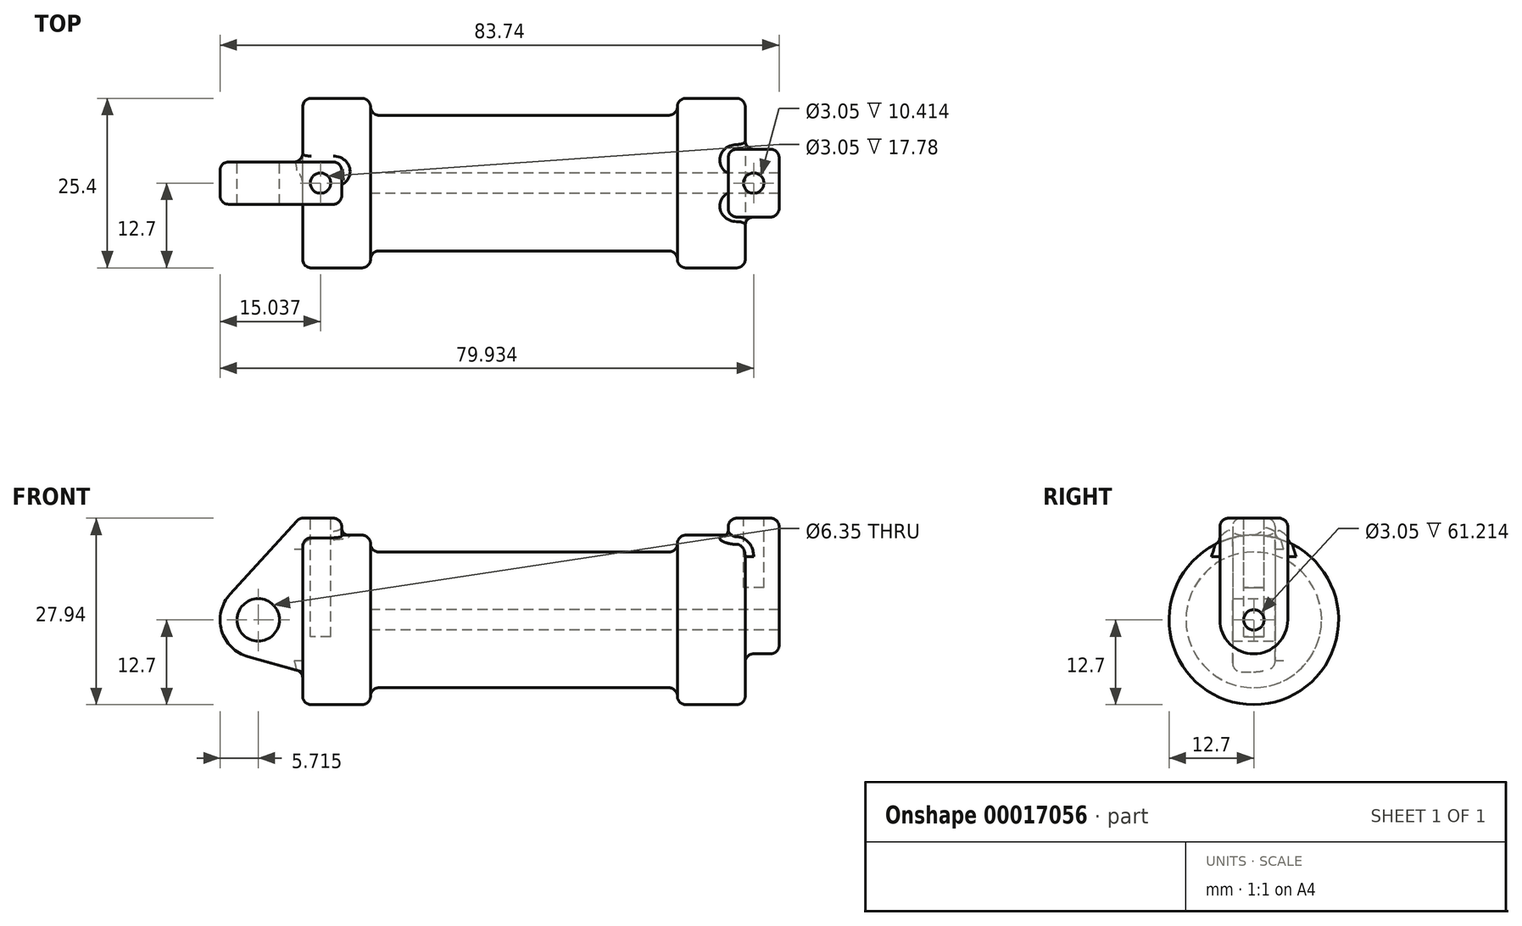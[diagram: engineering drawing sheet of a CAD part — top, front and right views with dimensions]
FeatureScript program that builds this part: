
annotation { "Feature Type Name" : "Feature", "Feature Type Description" : "" }
export const myFeature = defineFeature(function(context is Context, id is Id, definition is map)
    precondition{}
    {
        {
            var Q0;
            Q0=qCreatedBy(makeId("Front.planeOp"),FACE);
            var sketch = newSketch(context, id + "F0", { "sketchPlane" : qUnion([Q0])});
            skLineSegment(sketch, "E0", {"start": v(0, 0) * mm, "end": v(0, 12.7) * mm});
            skLineSegment(sketch, "E1", {"start": v(0, 12.7) * mm, "end": v(10.16, 12.7) * mm});
            skLineSegment(sketch, "E2", {"start": v(10.16, 12.7) * mm, "end": v(10.16, 10.16) * mm});
            skLineSegment(sketch, "E3", {"start": v(10.16, 10.16) * mm, "end": v(56.13, 10.16) * mm});
            skLineSegment(sketch, "E4", {"start": v(56.13, 10.16) * mm, "end": v(56.13, 12.7) * mm});
            skLineSegment(sketch, "E5", {"start": v(56.13, 12.7) * mm, "end": v(66.3, 12.7) * mm});
            skLineSegment(sketch, "E6", {"start": v(66.3, 12.7) * mm, "end": v(66.3, 0) * mm});
            skLineSegment(sketch, "E7", {"start": v(66.3, 0) * mm, "end": v(0, 0) * mm});
            skLineSegment(sketch, "E8", {"start": v(5.84, 15.24) * mm, "end": v(-0.5, 15.24) * mm});
            skLineSegment(sketch, "E9", {"start": v(-0.5, 15.24) * mm, "end": v(-10.88, 3.85) * mm});
            skLineSegment(sketch, "E10", {"start": v(0, 0) * mm, "end": v(-6.65, 0) * mm});
            skCircle(sketch, "E11", {"center": v(-6.65, 0) * mm, "radius": 5.72 * mm});
            skCircle(sketch, "E12", {"center": v(-6.65, 0) * mm, "radius": 3.18 * mm});
            skLineSegment(sketch, "E13", {"start": v(5.84, 15.24) * mm, "end": v(5.84, -9.4) * mm});
            skLineSegment(sketch, "E14", {"start": v(5.84, -9.4) * mm, "end": v(-8.18, -5.5) * mm});
            skSolve(sketch);
        }
        {
            var Q0;
            {var subQ6=sQuery(id+"F0.wireOp",EDGE,"E2");Q0=makeQuery(id+"F0.imprint","IMPRINT",FACE,{"disambiguationData":[TD([[makeQuery(id+"F0.imprint","IMPRINT",EDGE,{"derivedFrom":subQ6}),-1.0]])]});}
            var Q1;
            {var subQ5=sQuery(id+"F0.wireOp",EDGE,"E0");Q1=makeQuery(id+"F0.imprint","IMPRINT",FACE,{"disambiguationData":[TD([[makeQuery(id+"F0.imprint","IMPRINT",EDGE,{"derivedFrom":subQ5}),-1.0]])]});}
            var Q2;
            Q2=sQuery(id+"F0.wireOp",EDGE,"E7");
            revolve(context, id + "F1", {"entities" : qUnion([Q0, Q1]), "axis" : qUnion([Q2]), "revolveType" : RevolveType.FULL});
        }
        {
            var Q0;
            {var subQ8=sQuery(id+"F0.wireOp",EDGE,"E0");Q0=makeQuery(id+"F0.imprint","IMPRINT",FACE,{"disambiguationData":[TD([[makeQuery(id+"F0.imprint","IMPRINT",EDGE,{"derivedFrom":subQ8}),1.0]])]});}
            var Q1;
            {var subQ0=sQuery(id+"F0.wireOp",EDGE,"E12");Q1=makeQuery(id+"F0.imprint","IMPRINT",FACE,{"disambiguationData":[TD([[makeQuery(id+"F0.imprint","IMPRINT",EDGE,{"derivedFrom":subQ0}),-1.0]])]});}
            var Q2;
            {var subQ0=sQuery(id+"F0.wireOp",EDGE,"E14");Q2=makeQuery(id+"F0.imprint","IMPRINT",FACE,{"disambiguationData":[TD([[makeQuery(id+"F0.imprint","IMPRINT",EDGE,{"derivedFrom":subQ0}),-1.0]])]});}
            var Q3;
            {var subQ5=sQuery(id+"F0.wireOp",EDGE,"E0");Q3=makeQuery(id+"F0.imprint","IMPRINT",FACE,{"disambiguationData":[TD([[makeQuery(id+"F0.imprint","IMPRINT",EDGE,{"derivedFrom":subQ5}),-1.0]])]});}
            extrude(context, id + "F2", {"entities" : qUnion([Q0, Q1, Q2, Q3]), "operationType" : NewBodyOperationType.ADD, "endBound" : BoundingType.SYMMETRIC, "depth" : 6.35 * mm});
        }
        {
            var Q0;
            Q0=makeQuery(id+"F1.opRevolve","SWEPT_FACE",FACE,{"disambiguationData":[OSD([sQuery(id+"F0.wireOp",EDGE,"E6")])]});
            var sketch = newSketch(context, id + "F3", { "sketchPlane" : qUnion([Q0])});
            skCircle(sketch, "E15", {"center": v(0, 0) * mm, "radius": 5.08 * mm});
            skCircle(sketch, "E16", {"center": v(0, 0) * mm, "radius": 1.52 * mm});
            skLineSegment(sketch, "E17", {"start": v(-5.08, 0) * mm, "end": v(-5.08, 15.24) * mm});
            skLineSegment(sketch, "E18", {"start": v(-5.08, 15.24) * mm, "end": v(5.08, 15.24) * mm});
            skLineSegment(sketch, "E19", {"start": v(5.08, 15.24) * mm, "end": v(5.08, 0) * mm});
            skSolve(sketch);
        }
        {
            var Q0;
            Q0=makeQuery(id+"F3.imprint","IMPRINT",FACE,{"disambiguationData":[TD([[makeQuery(id+"F3.imprint","IMPRINT",EDGE,{"derivedFrom":sQuery(id+"F3.wireOp",EDGE,"E16")}),-1.0]])]});
            var Q1;
            {var subQ3=sQuery(id+"F3.wireOp",EDGE,"E17");var subQ5=sQuery(id+"F3.wireOp",EDGE,"E15");var subQ7=makeQuery(id+"F3.imprint","INTERSECT",VERTEX,{"derivedFrom":[subQ5,subQ3]});Q1=makeQuery(id+"F3.imprint","IMPRINT",FACE,{"disambiguationData":[TD([[makeQuery(id+"F3.imprint","IMPRINT",EDGE,{"disambiguationData":[TD([[subQ7,1.0]])],"derivedFrom":subQ5}),-1.0]])]});}
            var Q2;
            {var subQ5=sQuery(id+"F3.wireOp",EDGE,"E18");Q2=makeQuery(id+"F3.imprint","IMPRINT",FACE,{"disambiguationData":[TD([[makeQuery(id+"F3.imprint","IMPRINT",EDGE,{"derivedFrom":subQ5}),-1.0]])]});}
            extrude(context, id + "F4", {"entities" : qUnion([Q0, Q1, Q2]), "operationType" : NewBodyOperationType.ADD, "depth" : 5.08 * mm});
        }
        {
            var Q0;
            {var subQ0=sQuery(id+"F3.wireOp",EDGE,"E15");var subQ3=sQuery(id+"F3.wireOp",EDGE,"E17");var subQ4=makeQuery(id+"F3.imprint","INTERSECT",VERTEX,{"derivedFrom":[subQ0,subQ3]});var subQ5=makeQuery(id+"F3.imprint","IMPRINT",EDGE,{"disambiguationData":[TD([[subQ4,1.0]])],"derivedFrom":subQ0});var subQ10=sQuery(id+"F3.wireOp",EDGE,"E18");Q0=qUnion([makeQuery(id+"F3.imprint","IMPRINT",FACE,{"disambiguationData":[TD([[makeQuery(id+"F3.imprint","IMPRINT",EDGE,{"derivedFrom":sQuery(id+"F3.wireOp",EDGE,"E16")}),-1.0]])]}),makeQuery(id+"F3.imprint","IMPRINT",FACE,{"disambiguationData":[TD([[makeQuery(id+"F3.imprint","IMPRINT",EDGE,{"derivedFrom":subQ10}),-1.0]])]}),makeQuery(id+"F3.imprint","IMPRINT",FACE,{"disambiguationData":[TD([[subQ5,-1.0]])]})]);}
            extrude(context, id + "F5", {"entities" : qUnion([Q0]), "operationType" : NewBodyOperationType.ADD, "oppositeDirection" : true, "depth" : 2.54 * mm});
        }
        {
            var Q0;
            Q0=makeQuery(id+"F4.boolean.opBoolean","SPLIT",FACE,{"disambiguationData":[TD([makeQuery(id+"F4.opExtrude","SWEPT_FACE",FACE,{"disambiguationData":[OSD([sQuery(id+"F3.wireOp",EDGE,"E16")])]})])],"derivedFrom":makeQuery(id+"F1.opRevolve","SWEPT_FACE",FACE,{"disambiguationData":[OSD([sQuery(id+"F0.wireOp",EDGE,"E6")])]})});
            var Q1;
            Q1=makeQuery(id+"F1.opRevolve","SWEPT_FACE",FACE,{"disambiguationData":[OSD([sQuery(id+"F0.wireOp",EDGE,"E2")])]});
            extrude(context, id + "F6", {"entities" : qUnion([Q0]), "operationType" : NewBodyOperationType.REMOVE, "endBound" : BoundingType.UP_TO_SURFACE, "oppositeDirection" : true, "endBoundEntityFace" : qUnion([Q1]), "depth" : 25.4 * mm});
        }
        {
            var Q0;
            {var subQ0=sQuery(id+"F3.wireOp",EDGE,"E18");Q0=makeQuery(id+"F5.boolean.opBoolean","MERGE",FACE,{"derivedFrom":[makeQuery(id+"F4.opExtrude","SWEPT_FACE",FACE,{"disambiguationData":[OSD([subQ0])]}),makeQuery(id+"F5.opExtrude","SWEPT_FACE",FACE,{"disambiguationData":[OSD([subQ0])]})]});}
            var sketch = newSketch(context, id + "F7", { "sketchPlane" : qUnion([Q0])});
            skLineSegment(sketch, "E20", {"start": v(63.75, -5.08) * mm, "end": v(71.37, 5.08) * mm, "construction": true});
            skCircle(sketch, "E21", {"center": v(67.56, 0) * mm, "radius": 1.52 * mm});
            skSolve(sketch);
        }
        {
            var Q0;
            Q0=qSketchRegion(id+"F7",true);
            extrude(context, id + "F8", {"entities" : qUnion([Q0]), "operationType" : NewBodyOperationType.REMOVE, "oppositeDirection" : true, "depth" : 10.4 * mm});
        }
        {
            var Q0;
            Q0=makeQuery(id+"F2.opExtrude","SWEPT_FACE",FACE,{"disambiguationData":[OSD([sQuery(id+"F0.wireOp",EDGE,"E8")])]});
            var sketch = newSketch(context, id + "F9", { "sketchPlane" : qUnion([Q0])});
            skLineSegment(sketch, "E22", {"start": v(-0.5, -3.18) * mm, "end": v(5.84, 3.18) * mm, "construction": true});
            skCircle(sketch, "E23", {"center": v(2.67, 0) * mm, "radius": 1.52 * mm});
            skSolve(sketch);
        }
        {
            var Q0;
            Q0=makeQuery(id+"F9.imprint","IMPRINT",FACE,{"disambiguationData":[TD([[makeQuery(id+"F9.imprint","IMPRINT",EDGE,{"derivedFrom":sQuery(id+"F9.wireOp",EDGE,"E23")}),1.0]])]});
            extrude(context, id + "F10", {"entities" : qUnion([Q0]), "operationType" : NewBodyOperationType.REMOVE, "oppositeDirection" : true, "depth" : 17.78 * mm});
        }
        {
            var Q0;
            Q0=makeQuery(id+"F1.opRevolve","SWEPT_EDGE",EDGE,{"disambiguationData":[OSD([sQuery(id+"F0.wireOp",EDGE,"E2"),sQuery(id+"F0.wireOp",EDGE,"E3")])]});
            var Q1;
            Q1=makeQuery(id+"F1.opRevolve","SWEPT_EDGE",EDGE,{"disambiguationData":[OSD([sQuery(id+"F0.wireOp",EDGE,"E3"),sQuery(id+"F0.wireOp",EDGE,"E4")])]});
            fillet(context, id + "F11", {"entities" : qUnion([Q0, Q1]), "radius" : 1.27 * mm, "tangentPropagation" : true, "allowEdgeOverflow" : false});
        }
        {
            var Q0;
            Q0=makeQuery(id+"F2.opExtrude","SWEPT_EDGE",EDGE,{"disambiguationData":[OSD([sQuery(id+"F0.wireOp",EDGE,"E8"),sQuery(id+"F0.wireOp",EDGE,"E9")])]});
            var Q1;
            Q1=makeQuery(id+"F2.opExtrude","SWEPT_EDGE",EDGE,{"disambiguationData":[OSD([sQuery(id+"F0.wireOp",EDGE,"E8"),sQuery(id+"F0.wireOp",EDGE,"E13")])]});
            var Q2;
            Q2=makeQuery(id+"F2.opExtrude","CAP_EDGE",EDGE,{"disambiguationData":[OSD([sQuery(id+"F0.wireOp",EDGE,"E9")])],"isStart":false});
            var Q3;
            Q3=makeQuery(id+"F1.opRevolve","SWEPT_EDGE",EDGE,{"disambiguationData":[OSD([sQuery(id+"F0.wireOp",EDGE,"E0"),sQuery(id+"F0.wireOp",EDGE,"E1")])]});
            var Q4;
            Q4=makeQuery(id+"F1.opRevolve","SWEPT_EDGE",EDGE,{"disambiguationData":[OSD([sQuery(id+"F0.wireOp",EDGE,"E1"),sQuery(id+"F0.wireOp",EDGE,"E2")])]});
            var Q5;
            Q5=makeQuery(id+"F2.opExtrude","CAP_EDGE",EDGE,{"disambiguationData":[OSD([sQuery(id+"F0.wireOp",EDGE,"E13")])],"isStart":false});
            var Q6;
            Q6=makeQuery(id+"F2.opExtrude","CAP_EDGE",EDGE,{"disambiguationData":[OSD([sQuery(id+"F0.wireOp",EDGE,"E9")])],"isStart":true});
            var Q7;
            Q7=makeQuery(id+"F2.boolean.opBoolean","INTERSECT",EDGE,{"derivedFrom":[makeQuery(id+"F1.opRevolve","SWEPT_FACE",FACE,{"disambiguationData":[OSD([sQuery(id+"F0.wireOp",EDGE,"E1")])]}),makeQuery(id+"F2.opExtrude","CAP_FACE",FACE,{"disambiguationData":[OSD([sQuery(id+"F0.wireOp",EDGE,"E8"),sQuery(id+"F0.wireOp",EDGE,"E9"),sQuery(id+"F0.wireOp",EDGE,"E11"),sQuery(id+"F0.wireOp",EDGE,"E12"),sQuery(id+"F0.wireOp",EDGE,"E13"),sQuery(id+"F0.wireOp",EDGE,"E14")])],"isStart":true})]});
            var Q8;
            Q8=makeQuery(id+"F2.boolean.opBoolean","INTERSECT",EDGE,{"derivedFrom":[makeQuery(id+"F1.opRevolve","SWEPT_FACE",FACE,{"disambiguationData":[OSD([sQuery(id+"F0.wireOp",EDGE,"E0")])]}),makeQuery(id+"F2.opExtrude","CAP_FACE",FACE,{"disambiguationData":[OSD([sQuery(id+"F0.wireOp",EDGE,"E8"),sQuery(id+"F0.wireOp",EDGE,"E9"),sQuery(id+"F0.wireOp",EDGE,"E11"),sQuery(id+"F0.wireOp",EDGE,"E12"),sQuery(id+"F0.wireOp",EDGE,"E13"),sQuery(id+"F0.wireOp",EDGE,"E14")])],"isStart":true})]});
            var Q9;
            Q9=makeQuery(id+"F2.opExtrude","CAP_EDGE",EDGE,{"disambiguationData":[OSD([sQuery(id+"F0.wireOp",EDGE,"E8")])],"isStart":true});
            var Q10;
            Q10=makeQuery(id+"F2.opExtrude","CAP_EDGE",EDGE,{"disambiguationData":[OSD([sQuery(id+"F0.wireOp",EDGE,"E13")])],"isStart":true});
            var Q11;
            Q11=makeQuery(id+"F2.opExtrude","CAP_EDGE",EDGE,{"disambiguationData":[OSD([sQuery(id+"F0.wireOp",EDGE,"E8")])],"isStart":false});
            fillet(context, id + "F12", {"entities" : qUnion([Q0, Q1, Q2, Q3, Q4, Q5, Q6, Q7, Q8, Q9, Q10, Q11]), "radius" : 1.27 * mm, "tangentPropagation" : true, "allowEdgeOverflow" : false});
        }
        {
            var Q0;
            {var subQ0=sQuery(id+"F3.wireOp",EDGE,"E17");Q0=makeQuery(id+"F5.boolean.opBoolean","MERGE",FACE,{"derivedFrom":[makeQuery(id+"F4.opExtrude","SWEPT_FACE",FACE,{"disambiguationData":[OSD([subQ0])]}),makeQuery(id+"F5.opExtrude","SWEPT_FACE",FACE,{"disambiguationData":[OSD([subQ0])]})]});}
            var Q1;
            {var subQ0=sQuery(id+"F3.wireOp",EDGE,"E19");Q1=makeQuery(id+"F5.boolean.opBoolean","MERGE",FACE,{"derivedFrom":[makeQuery(id+"F4.opExtrude","SWEPT_FACE",FACE,{"disambiguationData":[OSD([subQ0])]}),makeQuery(id+"F5.opExtrude","SWEPT_FACE",FACE,{"disambiguationData":[OSD([subQ0])]})]});}
            var Q2;
            Q2=makeQuery(id+"F4.opExtrude","CAP_EDGE",EDGE,{"disambiguationData":[OSD([sQuery(id+"F3.wireOp",EDGE,"E18")])],"isStart":false});
            var Q3;
            Q3=makeQuery(id+"F5.opExtrude","CAP_EDGE",EDGE,{"disambiguationData":[OSD([sQuery(id+"F3.wireOp",EDGE,"E18")])],"isStart":false});
            var Q4;
            Q4=makeQuery(id+"F4.boolean.opBoolean","SPLIT",FACE,{"disambiguationData":[TD([makeQuery(id+"F1.opRevolve","SWEPT_FACE",FACE,{"disambiguationData":[OSD([sQuery(id+"F0.wireOp",EDGE,"E5")])]})])],"derivedFrom":makeQuery(id+"F1.opRevolve","SWEPT_FACE",FACE,{"disambiguationData":[OSD([sQuery(id+"F0.wireOp",EDGE,"E6")])]})});
            var Q5;
            Q5=makeQuery(id+"F1.opRevolve","SWEPT_EDGE",EDGE,{"disambiguationData":[OSD([sQuery(id+"F0.wireOp",EDGE,"E4"),sQuery(id+"F0.wireOp",EDGE,"E5")])]});
            fillet(context, id + "F13", {"entities" : qUnion([Q0, Q1, Q2, Q3, Q4, Q5]), "radius" : 1.27 * mm, "tangentPropagation" : true, "allowEdgeOverflow" : false});
        }
    });
